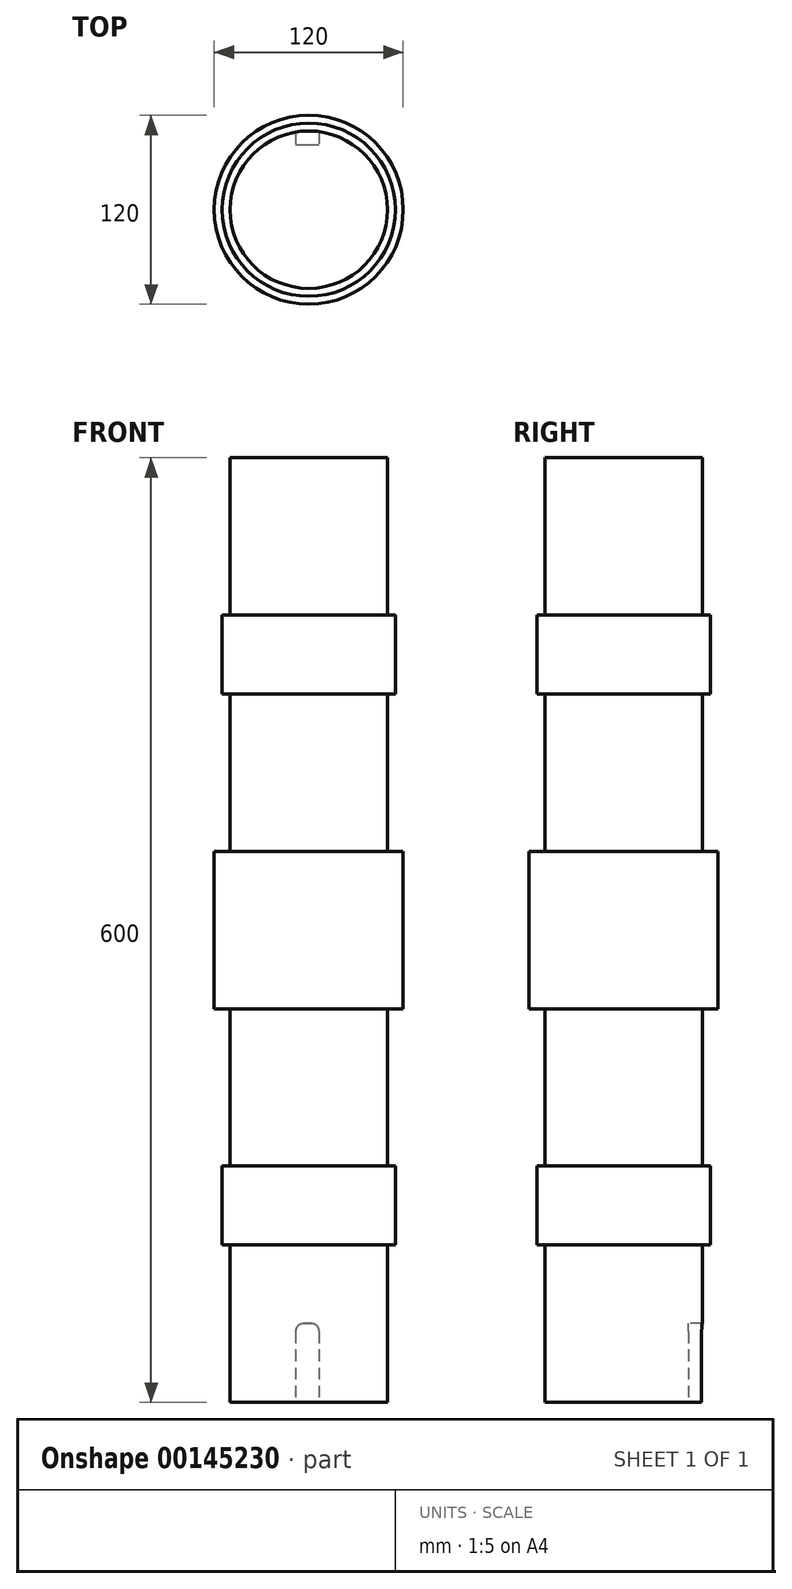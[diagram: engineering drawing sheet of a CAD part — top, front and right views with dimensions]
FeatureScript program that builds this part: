
annotation { "Feature Type Name" : "Feature", "Feature Type Description" : "" }
export const myFeature = defineFeature(function(context is Context, id is Id, definition is map)
    precondition{}
    {
        {
            var Q0;
            Q0=qCreatedBy(makeId("Right.planeOp"),FACE);
            var sketch = newSketch(context, id + "F0", { "sketchPlane" : qUnion([Q0])});
            skLineSegment(sketch, "E0", {"start": v(0, -300) * mm, "end": v(0, 300) * mm, "construction": true});
            skLineSegment(sketch, "E1", {"start": v(-55, -200) * mm, "end": v(-55, -150) * mm});
            skLineSegment(sketch, "E2", {"start": v(-55, -150) * mm, "end": v(-50, -150) * mm});
            skLineSegment(sketch, "E3", {"start": v(-50, -150) * mm, "end": v(-50, -50) * mm});
            skLineSegment(sketch, "E4", {"start": v(-50, -50) * mm, "end": v(-60, -50) * mm});
            skLineSegment(sketch, "E5", {"start": v(-60, 50) * mm, "end": v(-50, 50) * mm});
            skLineSegment(sketch, "E6", {"start": v(-50, 50) * mm, "end": v(-50, 150) * mm});
            skLineSegment(sketch, "E7", {"start": v(-50, 150) * mm, "end": v(-55, 150) * mm});
            skLineSegment(sketch, "E8", {"start": v(-55, 150) * mm, "end": v(-55, 200) * mm});
            skLineSegment(sketch, "E9", {"start": v(-55, 200) * mm, "end": v(-50, 200) * mm});
            skLineSegment(sketch, "E10", {"start": v(-50, 200) * mm, "end": v(-50, 300) * mm});
            skLineSegment(sketch, "E11", {"start": v(-50, 300) * mm, "end": v(0, 300) * mm});
            skLineSegment(sketch, "E12", {"start": v(-50, -200) * mm, "end": v(-55, -200) * mm});
            skLineSegment(sketch, "E13", {"start": v(-50, -200) * mm, "end": v(-50, -300) * mm});
            skLineSegment(sketch, "E14", {"start": v(-50, -300) * mm, "end": v(0, -300) * mm});
            skLineSegment(sketch, "E15", {"start": v(0, 300) * mm, "end": v(0, -300) * mm});
            skPoint(sketch, "E16.orphan", {"position": v(-60, 0) * mm});
            skLineSegment(sketch, "E17", {"start": v(-60, -50) * mm, "end": v(-60, 50) * mm});
            skSolve(sketch);
        }
        {
            var Q0;
            Q0 = qSketchRegion(id + "F0", true);
            var Q1;
            Q1=sQuery(id+"F0.wireOp",EDGE,"E15");
            revolve(context, id + "F1", {"entities" : qUnion([Q0]), "axis" : qUnion([Q1]), "revolveType" : RevolveType.FULL});
        }
        {
            var Q0;
            Q0=makeQuery(id+"F1.opRevolve","SWEPT_FACE",FACE,{"disambiguationData":[OSD([sQuery(id+"F0.wireOp",EDGE,"E14")])]});
            var sketch = newSketch(context, id + "F2", { "sketchPlane" : qUnion([Q0])});
            skLineSegment(sketch, "E18", {"start": v(0, 75.24) * mm, "end": v(0, -81.2) * mm, "construction": true});
            skArc(sketch, "E19.0", {"start": v(-8.34, -49.3) * mm, "mid": v(-0.85, -50) * mm, "end": v(6.66, -49.55) * mm});
            skLineSegment(sketch, "E20.top", {"start": v(-8.34, -41.3) * mm, "end": v(6.66, -41.3) * mm});
            skLineSegment(sketch, "E20.left", {"start": v(-8.34, -49.3) * mm, "end": v(-8.34, -41.3) * mm});
            skLineSegment(sketch, "E20.right", {"start": v(6.66, -49.55) * mm, "end": v(6.66, -41.3) * mm});
            skPoint(sketch, "E20.middle", {"position": v(0, -50) * mm});
            skSolve(sketch);
        }
        {
            var Q0;
            Q0 = qSketchRegion(id + "F2", true);
            extrude(context, id + "F3", {"entities" : qUnion([Q0]), "operationType" : NewBodyOperationType.REMOVE, "oppositeDirection" : true, "depth" : 50 * mm});
        }
        {
            var Q0;
            Q0=makeQuery(id+"F3.boolean.opBoolean","COPY",EDGE,{"derivedFrom":makeQuery(id+"F3.opExtrude","CAP_EDGE",EDGE,{"disambiguationData":[OSD([sQuery(id+"F2.wireOp",EDGE,"E20.right")])],"isStart":false})});
            var Q1;
            Q1=makeQuery(id+"F3.boolean.opBoolean","COPY",EDGE,{"derivedFrom":makeQuery(id+"F3.opExtrude","CAP_EDGE",EDGE,{"disambiguationData":[OSD([sQuery(id+"F2.wireOp",EDGE,"E20.left")])],"isStart":false})});
            fillet(context, id + "F4", {"entities" : qUnion([Q0, Q1]), "radius" : 5 * mm, "tangentPropagation" : true, "allowEdgeOverflow" : false});
        }
    });
